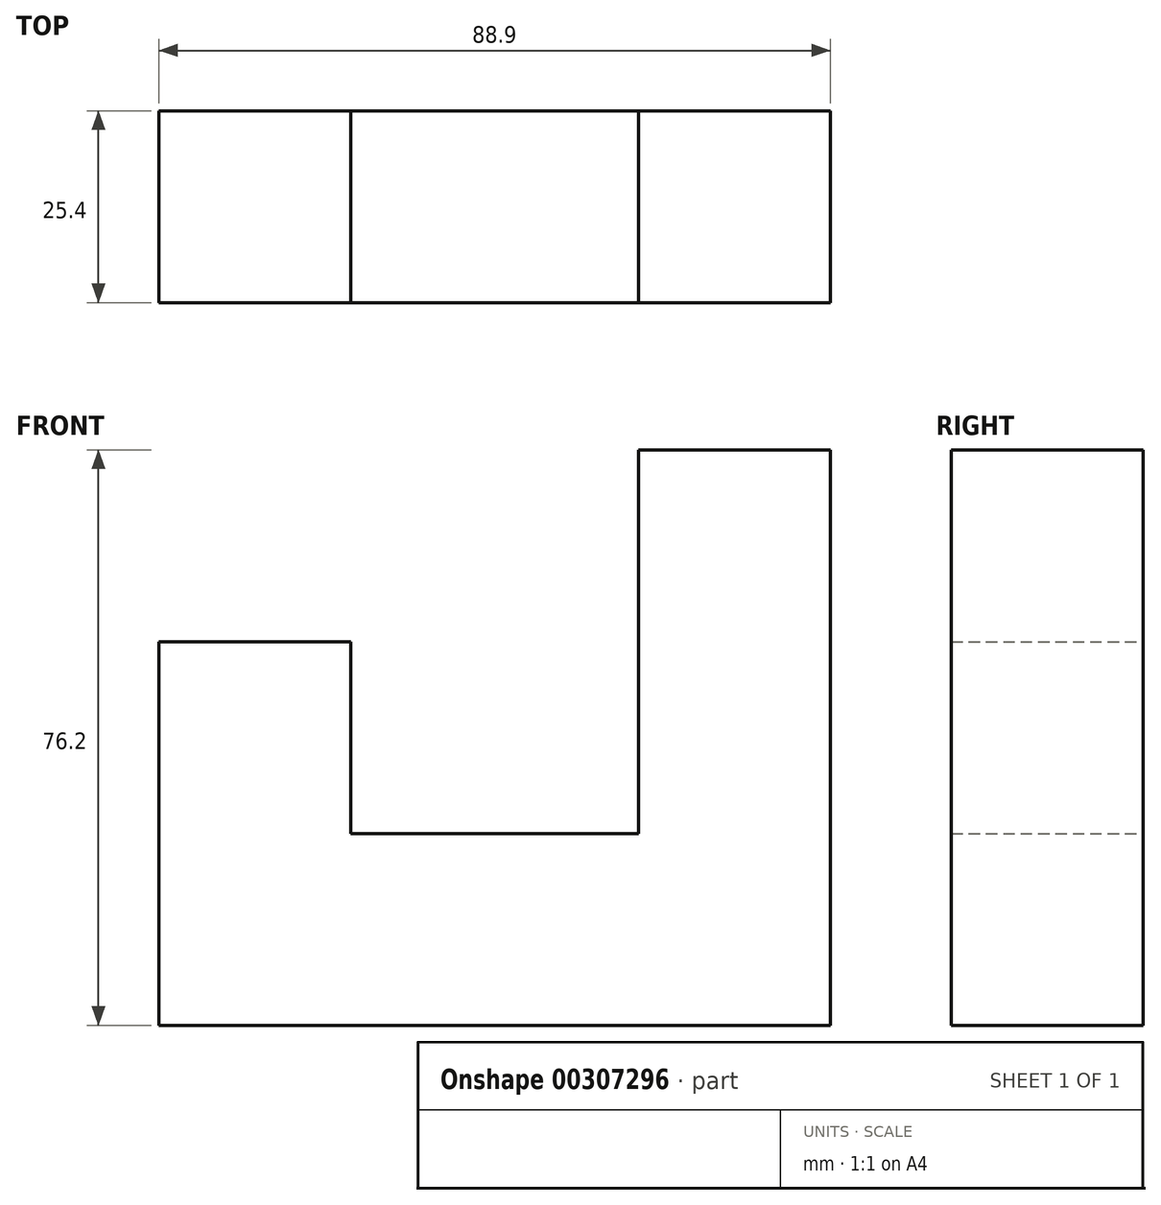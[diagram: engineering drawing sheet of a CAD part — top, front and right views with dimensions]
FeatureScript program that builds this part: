
annotation { "Feature Type Name" : "Feature", "Feature Type Description" : "" }
export const myFeature = defineFeature(function(context is Context, id is Id, definition is map)
    precondition{}
    {
        {
            var Q0;
            Q0=qCreatedBy(makeId("Front.planeOp"),FACE);
            var sketch = newSketch(context, id + "F0", { "sketchPlane" : qUnion([Q0])});
            skLineSegment(sketch, "E0", {"start": v(-50.38, -37.6) * mm, "end": v(38.52, -37.6) * mm});
            skLineSegment(sketch, "E1", {"start": v(38.52, -37.6) * mm, "end": v(38.52, 38.6) * mm});
            skLineSegment(sketch, "E2", {"start": v(38.52, 38.6) * mm, "end": v(13.12, 38.6) * mm});
            skLineSegment(sketch, "E3", {"start": v(13.12, 38.6) * mm, "end": v(13.12, -12.2) * mm});
            skLineSegment(sketch, "E4", {"start": v(13.12, -12.2) * mm, "end": v(-24.98, -12.2) * mm});
            skLineSegment(sketch, "E5", {"start": v(-24.98, -12.2) * mm, "end": v(-24.98, 13.2) * mm});
            skLineSegment(sketch, "E6", {"start": v(-24.98, 13.2) * mm, "end": v(-50.38, 13.2) * mm});
            skLineSegment(sketch, "E7", {"start": v(-50.38, 13.2) * mm, "end": v(-50.38, -37.6) * mm});
            skSolve(sketch);
        }
        {
            var Q0;
            Q0=makeQuery(id+"F0.imprint","IMPRINT",FACE,{"disambiguationData":[TD([[makeQuery(id+"F0.imprint","IMPRINT",EDGE,{"derivedFrom":sQuery(id+"F0.wireOp",EDGE,"E0")}),1.0]])]});
            extrude(context, id + "F1", {"entities" : qUnion([Q0]), "depth" : 25.4 * mm});
        }
    });
